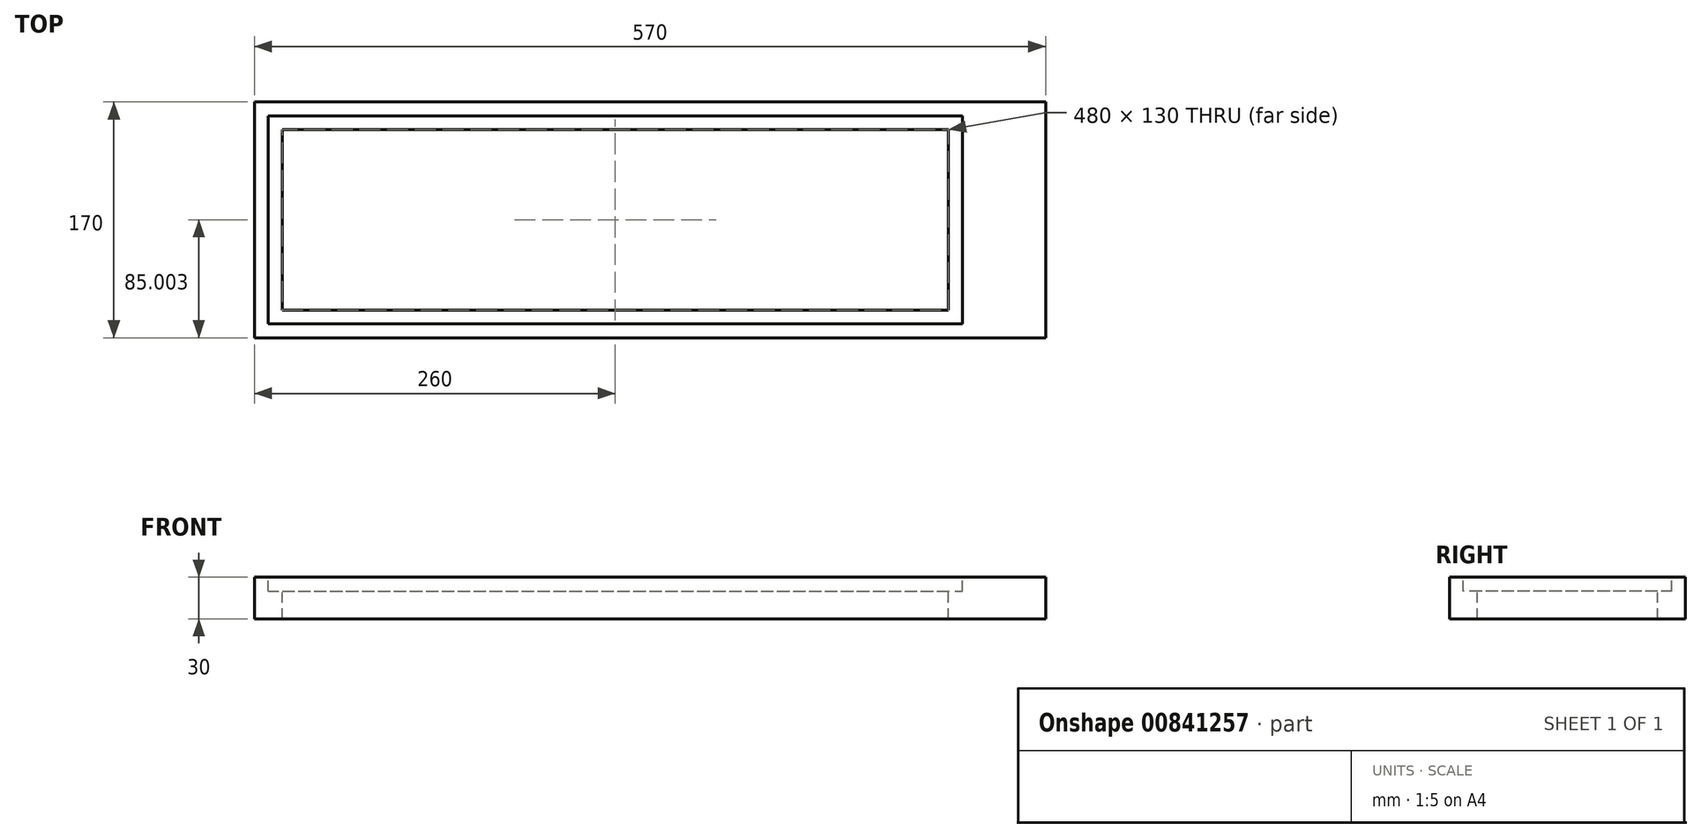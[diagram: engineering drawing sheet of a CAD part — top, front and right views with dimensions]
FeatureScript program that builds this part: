
annotation { "Feature Type Name" : "Feature", "Feature Type Description" : "" }
export const myFeature = defineFeature(function(context is Context, id is Id, definition is map)
    precondition{}
    {
        {
            var Q0;
            Q0=qCreatedBy(makeId("Top.planeOp"),FACE);
            var sketch = newSketch(context, id + "F0", { "sketchPlane" : qUnion([Q0])});
            skLineSegment(sketch, "E0.bottom", {"start": v(-273.8, 67.38) * mm, "end": v(296.2, 67.38) * mm});
            skLineSegment(sketch, "E0.top", {"start": v(-273.8, -102.62) * mm, "end": v(296.2, -102.62) * mm});
            skLineSegment(sketch, "E0.left", {"start": v(-273.8, 67.38) * mm, "end": v(-273.8, -102.62) * mm});
            skLineSegment(sketch, "E0.right", {"start": v(296.2, 67.38) * mm, "end": v(296.2, -102.62) * mm});
            skSolve(sketch);
        }
        {
            var Q0;
            Q0 = qSketchRegion(id + "F0", true);
            extrude(context, id + "F1", {"entities" : qUnion([Q0]), "oppositeDirection" : true, "depth" : 30 * mm, "offsetDistance" : 25 * mm});
        }
        {
            var Q0;
            Q0=makeQuery(id+"F1.opExtrude","CAP_FACE",FACE,{"disambiguationData":[OSD([sQuery(id+"F0.wireOp",EDGE,"E0.bottom"),sQuery(id+"F0.wireOp",EDGE,"E0.top"),sQuery(id+"F0.wireOp",EDGE,"E0.left"),sQuery(id+"F0.wireOp",EDGE,"E0.right")])],"isStart":true});
            var sketch = newSketch(context, id + "F2", { "sketchPlane" : qUnion([Q0])});
            skLineSegment(sketch, "E1.bottom", {"start": v(-263.8, 57.38) * mm, "end": v(236.2, 57.38) * mm});
            skLineSegment(sketch, "E1.top", {"start": v(-263.8, -92.62) * mm, "end": v(236.2, -92.62) * mm});
            skLineSegment(sketch, "E1.left", {"start": v(-263.8, 57.38) * mm, "end": v(-263.8, -92.62) * mm});
            skLineSegment(sketch, "E1.right", {"start": v(236.2, 57.38) * mm, "end": v(236.2, -92.62) * mm});
            skSolve(sketch);
        }
        {
            var Q0;
            Q0 = qSketchRegion(id + "F2", true);
            extrude(context, id + "F3", {"entities" : qUnion([Q0]), "operationType" : NewBodyOperationType.REMOVE, "oppositeDirection" : true, "depth" : 10 * mm, "offsetDistance" : 25 * mm});
        }
        {
            var Q0;
            Q0=makeQuery(id+"F3.boolean.opBoolean","COPY",FACE,{"derivedFrom":makeQuery(id+"F3.opExtrude","CAP_FACE",FACE,{"disambiguationData":[OSD([sQuery(id+"F2.wireOp",EDGE,"E1.bottom"),sQuery(id+"F2.wireOp",EDGE,"E1.top"),sQuery(id+"F2.wireOp",EDGE,"E1.left"),sQuery(id+"F2.wireOp",EDGE,"E1.right")])],"isStart":false})});
            var sketch = newSketch(context, id + "F4", { "sketchPlane" : qUnion([Q0])});
            skLineSegment(sketch, "E2.bottom", {"start": v(-253.8, 47.38) * mm, "end": v(226.2, 47.38) * mm});
            skLineSegment(sketch, "E2.top", {"start": v(-253.8, -82.62) * mm, "end": v(226.2, -82.62) * mm});
            skLineSegment(sketch, "E2.left", {"start": v(-253.8, 47.38) * mm, "end": v(-253.8, -82.62) * mm});
            skLineSegment(sketch, "E2.right", {"start": v(226.2, 47.38) * mm, "end": v(226.2, -82.62) * mm});
            skSolve(sketch);
        }
        {
            var Q0;
            Q0 = qSketchRegion(id + "F4", true);
            extrude(context, id + "F5", {"entities" : qUnion([Q0]), "operationType" : NewBodyOperationType.REMOVE, "endBound" : BoundingType.UP_TO_NEXT, "oppositeDirection" : true, "depth" : 25 * mm, "offsetDistance" : 25 * mm});
        }
    });
